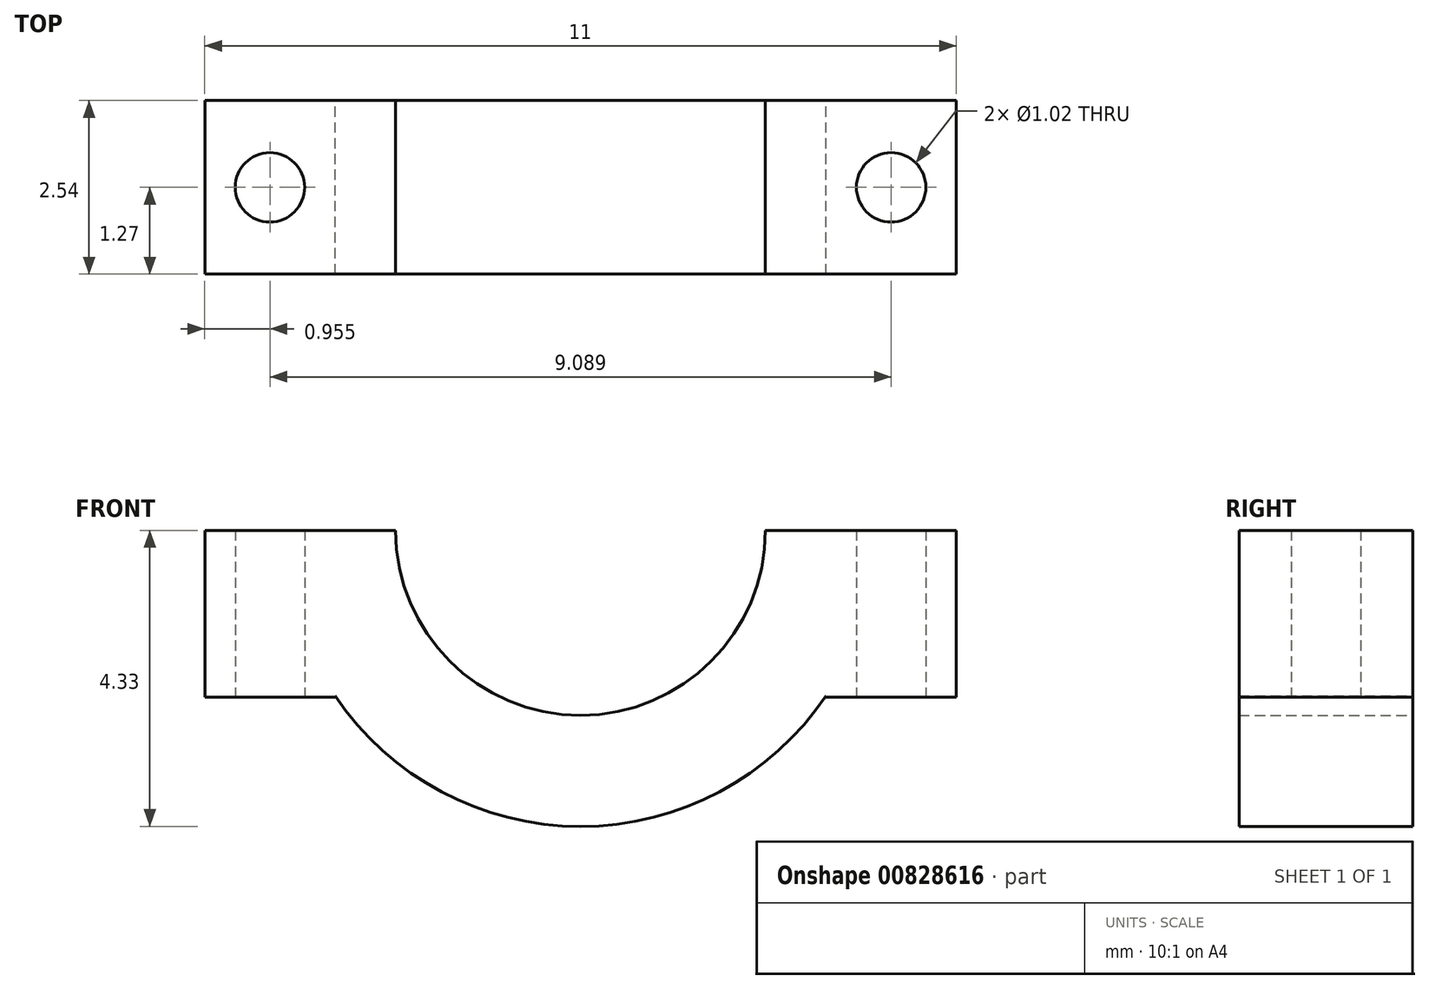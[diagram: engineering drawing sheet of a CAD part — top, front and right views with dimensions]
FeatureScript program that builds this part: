
annotation { "Feature Type Name" : "Feature", "Feature Type Description" : "" }
export const myFeature = defineFeature(function(context is Context, id is Id, definition is map)
    precondition{}
    {
        {
            var Q0;
            Q0=qCreatedBy(makeId("Front.planeOp"),FACE);
            var sketch = newSketch(context, id + "F0", { "sketchPlane" : qUnion([Q0])});
            skCircle(sketch, "E0", {"center": v(0, 0) * mm, "radius": 4.33 * mm});
            skCircle(sketch, "E1", {"center": v(0, 0) * mm, "radius": 2.7 * mm});
            skLineSegment(sketch, "E2.bottom", {"start": v(-3.6, 0) * mm, "end": v(-5.5, 0) * mm});
            skLineSegment(sketch, "E2.top", {"start": v(-3.6, -2.44) * mm, "end": v(-5.5, -2.44) * mm});
            skLineSegment(sketch, "E2.left", {"start": v(-3.6, 0) * mm, "end": v(-3.6, -2.44) * mm});
            skLineSegment(sketch, "E2.right", {"start": v(-5.5, 0) * mm, "end": v(-5.5, -2.44) * mm});
            skLineSegment(sketch, "E3.MirrorCS", {"start": v(3.6, 0) * mm, "end": v(3.6, -2.44) * mm});
            skLineSegment(sketch, "E4.MirrorCS", {"start": v(3.6, 0) * mm, "end": v(5.5, 0) * mm});
            skLineSegment(sketch, "E5.MirrorCS", {"start": v(5.5, 0) * mm, "end": v(5.5, -2.44) * mm});
            skLineSegment(sketch, "E6.MirrorCS", {"start": v(3.6, -2.44) * mm, "end": v(5.5, -2.44) * mm});
            skLineSegment(sketch, "E7", {"start": v(0, 0) * mm, "end": v(4.33, 0) * mm});
            skLineSegment(sketch, "E8", {"start": v(4.33, 0) * mm, "end": v(-4.33, 0) * mm});
            skSolve(sketch);
        }
        {
            var Q0;
            {var subQ1=sQuery(id+"F0.wireOp",EDGE,"E2.top");Q0=makeQuery(id+"F0.imprint","IMPRINT",FACE,{"disambiguationData":[TD([[makeQuery(id+"F0.imprint","IMPRINT",EDGE,{"derivedFrom":subQ1}),-1.0]])]});}
            var Q1;
            {var subQ0=sQuery(id+"F0.wireOp",EDGE,"E5.MirrorCS");Q1=makeQuery(id+"F0.imprint","IMPRINT",FACE,{"disambiguationData":[TD([[makeQuery(id+"F0.imprint","IMPRINT",EDGE,{"derivedFrom":subQ0}),-1.0]])]});}
            var Q2;
            {var subQ0=sQuery(id+"F0.wireOp",EDGE,"E2.bottom");var subQ1=sQuery(id+"F0.wireOp",EDGE,"E0");var subQ2=makeQuery(id+"F0.imprint","INTERSECT",VERTEX,{"derivedFrom":[subQ1,subQ0]});Q2=makeQuery(id+"F0.imprint","IMPRINT",FACE,{"disambiguationData":[TD([[makeQuery(id+"F0.imprint","IMPRINT",EDGE,{"disambiguationData":[TD([[subQ2,-1.0]])],"derivedFrom":subQ1}),1.0]])]});}
            var Q3;
            {var subQ0=sQuery(id+"F0.wireOp",EDGE,"E4.MirrorCS");var subQ1=sQuery(id+"F0.wireOp",EDGE,"E0");var subQ2=makeQuery(id+"F0.imprint","INTERSECT",VERTEX,{"derivedFrom":[subQ1,subQ0]});Q3=makeQuery(id+"F0.imprint","IMPRINT",FACE,{"disambiguationData":[TD([[makeQuery(id+"F0.imprint","IMPRINT",EDGE,{"disambiguationData":[TD([[subQ2,1.0]])],"derivedFrom":subQ1}),1.0]])]});}
            var Q4;
            {var subQ1=sQuery(id+"F0.wireOp",EDGE,"E3.MirrorCS");var subQ3=sQuery(id+"F0.wireOp",EDGE,"E0");var subQ4=makeQuery(id+"F0.imprint","INTERSECT",VERTEX,{"derivedFrom":[subQ3,subQ1]});Q4=makeQuery(id+"F0.imprint","IMPRINT",FACE,{"disambiguationData":[TD([[makeQuery(id+"F0.imprint","IMPRINT",EDGE,{"disambiguationData":[TD([[subQ4,1.0]])],"derivedFrom":subQ3}),1.0]])]});}
            extrude(context, id + "F1", {"entities" : qUnion([Q0, Q1, Q2, Q3, Q4]), "endBound" : BoundingType.SYMMETRIC, "depth" : 2.54 * mm, "offsetDistance" : 25.4 * mm});
        }
        {
            var Q0;
            Q0=makeQuery(id+"F1.opExtrude","SWEPT_FACE",FACE,{"disambiguationData":[OSD([sQuery(id+"F0.wireOp",EDGE,"E2.top")])]});
            var sketch = newSketch(context, id + "F2", { "sketchPlane" : qUnion([Q0])});
            skCircle(sketch, "E9", {"center": v(-4.54, 0) * mm, "radius": 0.5 * mm});
            skSolve(sketch);
        }
        {
            var Q0;
            Q0=makeQuery(id+"F1.opExtrude","SWEPT_FACE",FACE,{"disambiguationData":[OSD([sQuery(id+"F0.wireOp",EDGE,"E6.MirrorCS")])]});
            var sketch = newSketch(context, id + "F3", { "sketchPlane" : qUnion([Q0])});
            skCircle(sketch, "E10", {"center": v(4.54, 0) * mm, "radius": 0.5 * mm});
            skSolve(sketch);
        }
        {
            var Q0;
            Q0=makeQuery(id+"F3.imprint","IMPRINT",FACE,{"disambiguationData":[TD([[makeQuery(id+"F3.imprint","IMPRINT",EDGE,{"derivedFrom":sQuery(id+"F3.wireOp",EDGE,"E10")}),1.0]])]});
            var Q1;
            Q1=makeQuery(id+"F2.imprint","IMPRINT",FACE,{"disambiguationData":[TD([[makeQuery(id+"F2.imprint","IMPRINT",EDGE,{"derivedFrom":sQuery(id+"F2.wireOp",EDGE,"E9")}),1.0]])]});
            extrude(context, id + "F4", {"entities" : qUnion([Q0, Q1]), "operationType" : NewBodyOperationType.REMOVE, "oppositeDirection" : true, "depth" : 25.4 * mm, "offsetDistance" : 25.4 * mm});
        }
    });
